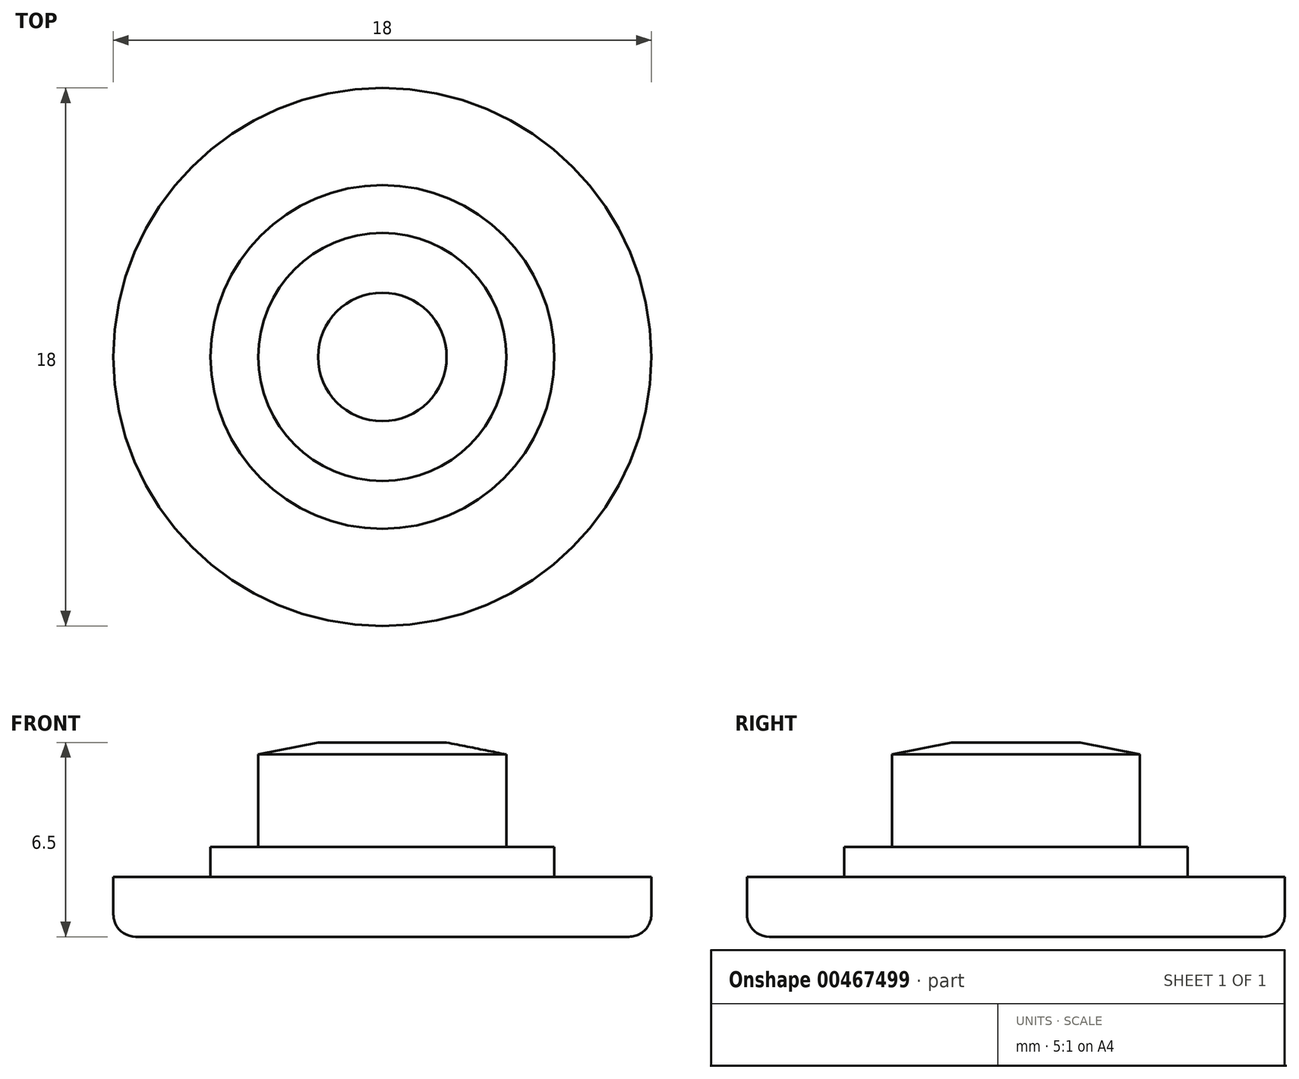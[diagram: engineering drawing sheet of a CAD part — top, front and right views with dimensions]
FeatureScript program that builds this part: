
annotation { "Feature Type Name" : "Feature", "Feature Type Description" : "" }
export const myFeature = defineFeature(function(context is Context, id is Id, definition is map)
    precondition{}
    {
        {
            var Q0;
            Q0=qCreatedBy(makeId("Top.planeOp"),FACE);
            var sketch = newSketch(context, id + "F0", { "sketchPlane" : qUnion([Q0])});
            skCircle(sketch, "E0", {"center": v(0, 0) * mm, "radius": 9 * mm});
            skSolve(sketch);
        }
        {
            var Q0;
            Q0=makeQuery(id+"F0.imprint","IMPRINT",FACE,{"disambiguationData":[TD([[makeQuery(id+"F0.imprint","IMPRINT",EDGE,{"derivedFrom":sQuery(id+"F0.wireOp",EDGE,"E0")}),1.0]])]});
            extrude(context, id + "F1", {"entities" : qUnion([Q0]), "depth" : 2 * mm, "offsetDistance" : 25 * mm});
        }
        {
            var Q0;
            Q0=makeQuery(id+"F1.opExtrude","CAP_FACE",FACE,{"disambiguationData":[OSD([sQuery(id+"F0.wireOp",EDGE,"E0")])],"isStart":false});
            var sketch = newSketch(context, id + "F2", { "sketchPlane" : qUnion([Q0])});
            skCircle(sketch, "E1", {"center": v(0, 0) * mm, "radius": 5.75 * mm});
            skSolve(sketch);
        }
        {
            var Q0;
            Q0=makeQuery(id+"F2.imprint","IMPRINT",FACE,{"disambiguationData":[TD([[makeQuery(id+"F2.imprint","IMPRINT",EDGE,{"derivedFrom":sQuery(id+"F2.wireOp",EDGE,"E1")}),1.0]])]});
            extrude(context, id + "F3", {"entities" : qUnion([Q0]), "operationType" : NewBodyOperationType.ADD, "depth" : 1 * mm});
        }
        {
            var Q0;
            Q0=makeQuery(id+"F3.opExtrude","CAP_FACE",FACE,{"disambiguationData":[OSD([sQuery(id+"F2.wireOp",EDGE,"E1")])],"isStart":false});
            var sketch = newSketch(context, id + "F4", { "sketchPlane" : qUnion([Q0])});
            skCircle(sketch, "E2", {"center": v(0, 0) * mm, "radius": 4.15 * mm});
            skSolve(sketch);
        }
        {
            var Q0;
            Q0=makeQuery(id+"F4.imprint","IMPRINT",FACE,{"disambiguationData":[TD([[makeQuery(id+"F4.imprint","IMPRINT",EDGE,{"derivedFrom":sQuery(id+"F4.wireOp",EDGE,"E2")}),1.0]])]});
            extrude(context, id + "F5", {"entities" : qUnion([Q0]), "operationType" : NewBodyOperationType.ADD, "depth" : 3.5 * mm, "offsetDistance" : 25 * mm});
        }
        {
            var Q0;
            Q0=makeQuery(id+"F1.opExtrude","CAP_EDGE",EDGE,{"disambiguationData":[OSD([sQuery(id+"F0.wireOp",EDGE,"E0")])],"isStart":true});
            fillet(context, id + "F6", {"entities" : qUnion([Q0]), "radius" : .75 * mm, "tangentPropagation" : true, "allowEdgeOverflow" : false});
        }
        {
            var Q0;
            Q0=makeQuery(id+"F5.opExtrude","CAP_EDGE",EDGE,{"disambiguationData":[OSD([sQuery(id+"F4.wireOp",EDGE,"E2")])],"isStart":false});
            chamfer(context, id + "F7", {"entities" : qUnion([Q0]), "chamferType" : ChamferType.TWO_OFFSETS, "width1" : .4 * mm, "oppositeDirection" : false, "width2" : 2 * mm, "tangentPropagation" : true});
        }
    });
